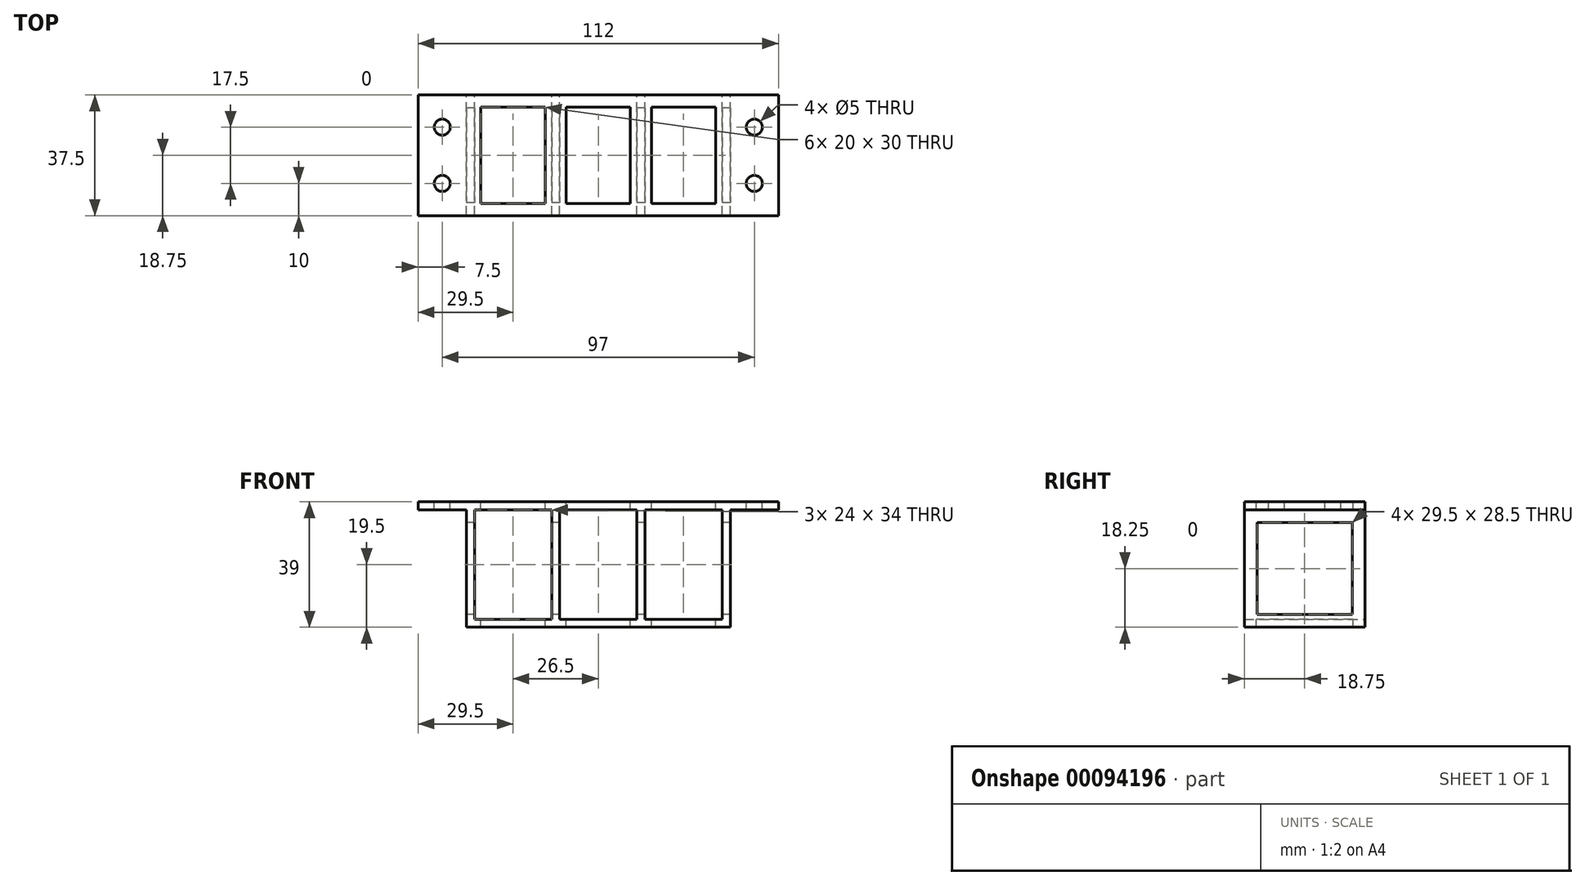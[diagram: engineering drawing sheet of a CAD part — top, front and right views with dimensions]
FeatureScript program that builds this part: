
annotation { "Feature Type Name" : "Feature", "Feature Type Description" : "" }
export const myFeature = defineFeature(function(context is Context, id is Id, definition is map)
    precondition{}
    {
        {
            var Q0;
            Q0=qCreatedBy(makeId("Front.planeOp"),FACE);
            var sketch = newSketch(context, id + "F0", { "sketchPlane" : qUnion([Q0])});
            skLineSegment(sketch, "E0.bottom", {"start": v(-12, 17) * mm, "end": v(12, 17) * mm});
            skLineSegment(sketch, "E0.top", {"start": v(-12, -17) * mm, "end": v(12, -17) * mm});
            skLineSegment(sketch, "E0.left", {"start": v(-12, 17) * mm, "end": v(-12, -17) * mm});
            skLineSegment(sketch, "E0.right", {"start": v(12, 17) * mm, "end": v(12, -17) * mm});
            skPoint(sketch, "E0.middle", {"position": v(0, 0) * mm});
            skLineSegment(sketch, "E1.bottom", {"start": v(-14.5, 19.5) * mm, "end": v(14.5, 19.5) * mm});
            skLineSegment(sketch, "E1.top", {"start": v(-14.5, -19.5) * mm, "end": v(14.5, -19.5) * mm});
            skLineSegment(sketch, "E1.left", {"start": v(-14.5, 19.5) * mm, "end": v(-14.5, -19.5) * mm});
            skLineSegment(sketch, "E2.MirrorCS", {"start": v(14.5, 17) * mm, "end": v(14.5, -17) * mm});
            skLineSegment(sketch, "E3.MirrorCS", {"start": v(38.5, 17) * mm, "end": v(14.5, 17) * mm});
            skLineSegment(sketch, "E4.MirrorCS", {"start": v(38.5, -17) * mm, "end": v(14.5, -17) * mm});
            skLineSegment(sketch, "E5.MirrorCS", {"start": v(38.5, 17) * mm, "end": v(38.5, -17) * mm});
            skLineSegment(sketch, "E6.MirrorCS", {"start": v(43.5, 19.5) * mm, "end": v(14.5, 19.5) * mm});
            skLineSegment(sketch, "E7.MirrorCS", {"start": v(43.5, -19.5) * mm, "end": v(14.5, -19.5) * mm});
            skLineSegment(sketch, "E8.MirrorCS", {"start": v(43.5, 19.5) * mm, "end": v(67.5, 19.5) * mm});
            skLineSegment(sketch, "E9.MirrorCS", {"start": v(41, 17) * mm, "end": v(65, 17) * mm});
            skLineSegment(sketch, "E10.MirrorCS", {"start": v(41, -17) * mm, "end": v(65, -17) * mm});
            skLineSegment(sketch, "E11.MirrorCS", {"start": v(41, 17) * mm, "end": v(41, -17) * mm});
            skLineSegment(sketch, "E12.MirrorCS", {"start": v(43.5, -19.5) * mm, "end": v(67.5, -19.5) * mm});
            skLineSegment(sketch, "E13.MirrorCS", {"start": v(65, 17) * mm, "end": v(65, -17) * mm});
            skLineSegment(sketch, "E14.MirrorCS", {"start": v(67.5, 19.5) * mm, "end": v(67.5, -19.5) * mm});
            skSolve(sketch);
        }
        {
            var Q0;
            Q0 = qSketchRegion(id + "F0", true);
            extrude(context, id + "F1", {"entities" : qUnion([Q0]), "depth" : 18.75 * mm, "hasSecondDirection" : true, "secondDirectionOppositeDirection" : true, "secondDirectionDepth" : 18.75 * mm});
        }
        {
            var Q0;
            Q0=makeQuery(id+"F1.opExtrude","SWEPT_FACE",FACE,{"disambiguationData":[OSD([sQuery(id+"F0.wireOp",EDGE,"E1.bottom")])]});
            var sketch = newSketch(context, id + "F2", { "sketchPlane" : qUnion([Q0])});
            skPoint(sketch, "E15.0.end.orphan", {"position": v(-14.5, -18.75) * mm});
            skPoint(sketch, "E16.bottom.start.orphan", {"position": v(-14.5, 18.75) * mm});
            skPoint(sketch, "E16.top.end.orphan", {"position": v(-29.5, -18.75) * mm});
            skPoint(sketch, "E17.right.end.orphan", {"position": v(82.5, -18.75) * mm});
            skLineSegment(sketch, "E18.bottom", {"start": v(-29.5, -18.75) * mm, "end": v(82.5, -18.75) * mm});
            skLineSegment(sketch, "E18.top", {"start": v(-29.5, 18.75) * mm, "end": v(82.5, 18.75) * mm});
            skLineSegment(sketch, "E18.left", {"start": v(-29.5, -18.75) * mm, "end": v(-29.5, 18.75) * mm});
            skLineSegment(sketch, "E18.right", {"start": v(82.5, -18.75) * mm, "end": v(82.5, 18.75) * mm});
            skLineSegment(sketch, "E19", {"start": v(-29.5, 18.75) * mm, "end": v(-14.5, 18.75) * mm});
            skPoint(sketch, "E20.centerSnap0", {"position": v(-22, 18.75) * mm});
            skCircle(sketch, "E21", {"center": v(-22, 8.75) * mm, "radius": 2.5 * mm});
            skCircle(sketch, "E22.MirrorC", {"center": v(-22, -8.75) * mm, "radius": 2.5 * mm});
            skLineSegment(sketch, "E23", {"start": v(26.5, 18.75) * mm, "end": v(26.5, -18.75) * mm, "construction": true});
            skCircle(sketch, "E24.MirrorC", {"center": v(75, 8.75) * mm, "radius": 2.5 * mm});
            skCircle(sketch, "E25.MirrorC", {"center": v(75, -8.75) * mm, "radius": 2.5 * mm});
            skLineSegment(sketch, "E26.bottom", {"start": v(-10, 15) * mm, "end": v(10, 15) * mm});
            skLineSegment(sketch, "E26.top", {"start": v(-10, -15) * mm, "end": v(10, -15) * mm});
            skLineSegment(sketch, "E26.left", {"start": v(-10, 15) * mm, "end": v(-10, -15) * mm});
            skLineSegment(sketch, "E26.right", {"start": v(10, 15) * mm, "end": v(10, -15) * mm});
            skPoint(sketch, "E26.middle", {"position": v(0, 0) * mm});
            skLineSegment(sketch, "E27.bottom", {"start": v(16.5, 15) * mm, "end": v(36.5, 15) * mm});
            skLineSegment(sketch, "E27.top", {"start": v(16.5, -15) * mm, "end": v(36.5, -15) * mm});
            skLineSegment(sketch, "E27.left", {"start": v(16.5, 15) * mm, "end": v(16.5, -15) * mm});
            skLineSegment(sketch, "E27.right", {"start": v(36.5, 15) * mm, "end": v(36.5, -15) * mm});
            skPoint(sketch, "E27.middle", {"position": v(26.5, 0) * mm});
            skLineSegment(sketch, "E28.MirrorCS", {"start": v(63, 15) * mm, "end": v(43, 15) * mm});
            skLineSegment(sketch, "E29.MirrorCS", {"start": v(43, 15) * mm, "end": v(43, -15) * mm});
            skLineSegment(sketch, "E30.MirrorCS", {"start": v(63, -15) * mm, "end": v(43, -15) * mm});
            skLineSegment(sketch, "E31.MirrorCS", {"start": v(63, 15) * mm, "end": v(63, -15) * mm});
            skSolve(sketch);
        }
        {
            var Q0;
            Q0 = qSketchRegion(id + "F2", true);
            extrude(context, id + "F3", {"entities" : qUnion([Q0]), "operationType" : NewBodyOperationType.ADD, "oppositeDirection" : true, "depth" : 2.5 * mm});
        }
        {
            var Q0;
            Q0=makeQuery(id+"F2.imprint","IMPRINT",FACE,{"disambiguationData":[TD([[makeQuery(id+"F2.imprint","IMPRINT",EDGE,{"derivedFrom":sQuery(id+"F2.wireOp",EDGE,"E26.bottom")}),-1.0]])]});
            var Q1;
            Q1=makeQuery(id+"F2.imprint","IMPRINT",FACE,{"disambiguationData":[TD([[makeQuery(id+"F2.imprint","IMPRINT",EDGE,{"derivedFrom":sQuery(id+"F2.wireOp",EDGE,"E28.MirrorCS")}),1.0]])]});
            var Q2;
            Q2=makeQuery(id+"F2.imprint","IMPRINT",FACE,{"disambiguationData":[TD([[makeQuery(id+"F2.imprint","IMPRINT",EDGE,{"derivedFrom":sQuery(id+"F2.wireOp",EDGE,"E27.bottom")}),-1.0]])]});
            extrude(context, id + "F4", {"entities" : qUnion([Q0, Q1, Q2]), "operationType" : NewBodyOperationType.REMOVE, "oppositeDirection" : true, "depth" : 60 * mm});
        }
        {
            var Q0;
            Q0=qCreatedBy(makeId("Right.planeOp"),FACE);
            var sketch = newSketch(context, id + "F5", { "sketchPlane" : qUnion([Q0])});
            skLineSegment(sketch, "E32.bottom", {"start": v(-14.75, 13) * mm, "end": v(14.75, 13) * mm});
            skLineSegment(sketch, "E32.top", {"start": v(-14.75, -15.5) * mm, "end": v(14.75, -15.5) * mm});
            skLineSegment(sketch, "E32.left", {"start": v(-14.75, 13) * mm, "end": v(-14.75, -15.5) * mm});
            skLineSegment(sketch, "E32.right", {"start": v(14.75, 13) * mm, "end": v(14.75, -15.5) * mm});
            skSolve(sketch);
        }
        {
            var Q0;
            Q0 = qSketchRegion(id + "F5", true);
            extrude(context, id + "F6", {"entities" : qUnion([Q0]), "operationType" : NewBodyOperationType.REMOVE, "depth" : 76.16 * mm, "hasSecondDirection" : true, "secondDirectionOppositeDirection" : true, "secondDirectionDepth" : 25 * mm});
        }
    });
